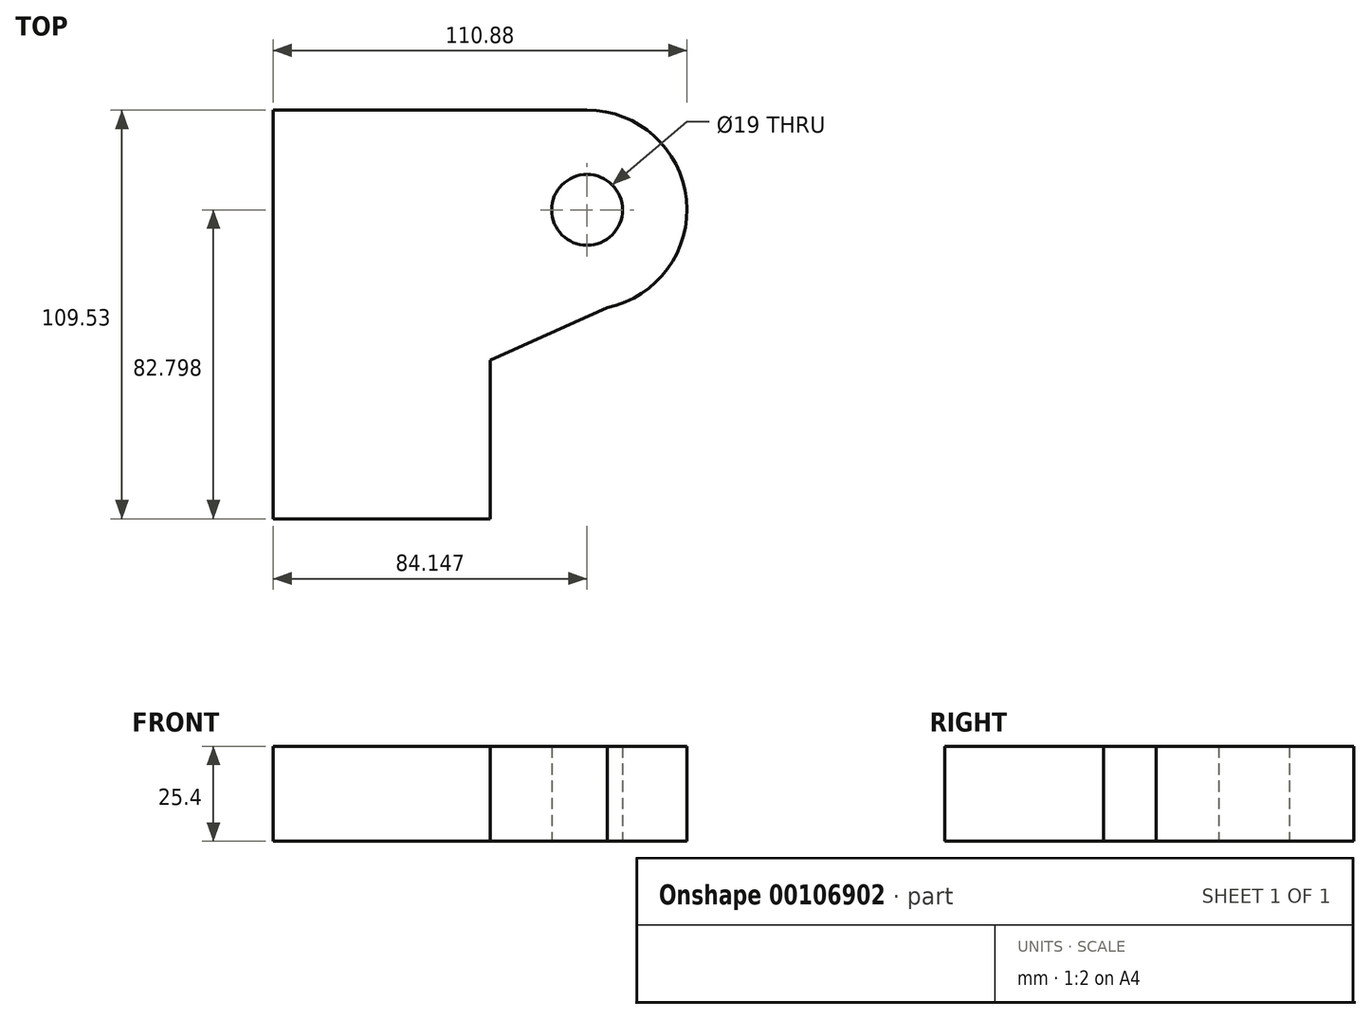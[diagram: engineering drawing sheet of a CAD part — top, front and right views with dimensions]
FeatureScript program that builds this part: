
annotation { "Feature Type Name" : "Feature", "Feature Type Description" : "" }
export const myFeature = defineFeature(function(context is Context, id is Id, definition is map)
    precondition{}
    {
        {
            var Q0;
            Q0=qCreatedBy(makeId("Top.planeOp"),FACE);
            var sketch = newSketch(context, id + "F0", { "sketchPlane" : qUnion([Q0])});
            skLineSegment(sketch, "E0.bottom", {"start": v(-77.01, 55.76) * mm, "end": v(76.44, 55.76) * mm});
            skLineSegment(sketch, "E0.top", {"start": v(-77.01, -56.9) * mm, "end": v(76.44, -56.9) * mm});
            skLineSegment(sketch, "E0.left", {"start": v(-77.01, 55.76) * mm, "end": v(-77.01, -56.9) * mm});
            skLineSegment(sketch, "E0.right", {"start": v(76.44, 55.76) * mm, "end": v(76.44, -56.9) * mm});
            skSolve(sketch);
        }
        {
            var Q0;
            Q0=makeQuery(id+"F0.imprint","IMPRINT",FACE,{"disambiguationData":[TD([[makeQuery(id+"F0.imprint","IMPRINT",EDGE,{"derivedFrom":sQuery(id+"F0.wireOp",EDGE,"E0.bottom")}),-1.0]])]});
            var sketch = newSketch(context, id + "F1", { "sketchPlane" : qUnion([Q0])});
            skSolve(sketch);
        }
        {
            var Q0;
            Q0=makeQuery(id+"F1.imprint","IMPRINT",FACE,{"disambiguationData":[TD([[makeQuery(id+"F1.imprint","IMPRINT",EDGE,{"derivedFrom":makeQuery(id+"F0.imprint","IMPRINT",EDGE,{"derivedFrom":sQuery(id+"F0.wireOp",EDGE,"E0.bottom")})}),-1.0]])]});
            var sketch = newSketch(context, id + "F2", { "sketchPlane" : qUnion([Q0])});
            skLineSegment(sketch, "E1", {"start": v(-58.19, 52.91) * mm, "end": v(-58.19, -45.09) * mm});
            skLineSegment(sketch, "E2.bottom", {"start": v(-58.19, -14.12) * mm, "end": v(0, -14.12) * mm});
            skLineSegment(sketch, "E2.top", {"start": v(-58.19, -56.62) * mm, "end": v(0, -56.62) * mm});
            skLineSegment(sketch, "E2.left", {"start": v(-58.19, -14.12) * mm, "end": v(-58.19, -56.62) * mm});
            skLineSegment(sketch, "E2.right", {"start": v(0, -14.12) * mm, "end": v(0, -56.62) * mm});
            skLineSegment(sketch, "E3", {"start": v(-36.51, -14.12) * mm, "end": v(-36.51, -58.9) * mm});
            skLineSegment(sketch, "E4", {"start": v(-26.81, -14.12) * mm, "end": v(-26.81, -56.62) * mm});
            skLineSegment(sketch, "E5", {"start": v(-58.19, 52.91) * mm, "end": v(25.96, 52.91) * mm});
            skArc(sketch, "E6", {"start": v(25.96, 52.91) * mm, "mid": v(52.55, 28.9) * mm, "end": v(31.38, 0) * mm});
            skLineSegment(sketch, "E7", {"start": v(31.38, 0) * mm, "end": v(0, -14.12) * mm});
            skCircle(sketch, "E8", {"center": v(25.96, 26.18) * mm, "radius": 9.5 * mm});
            skSolve(sketch);
        }
        {
            var Q0;
            Q0 = qSketchRegion(id + "F2", true);
            extrude(context, id + "F3", {"entities" : qUnion([Q0]), "depth" : 25.4 * mm});
        }
    });
